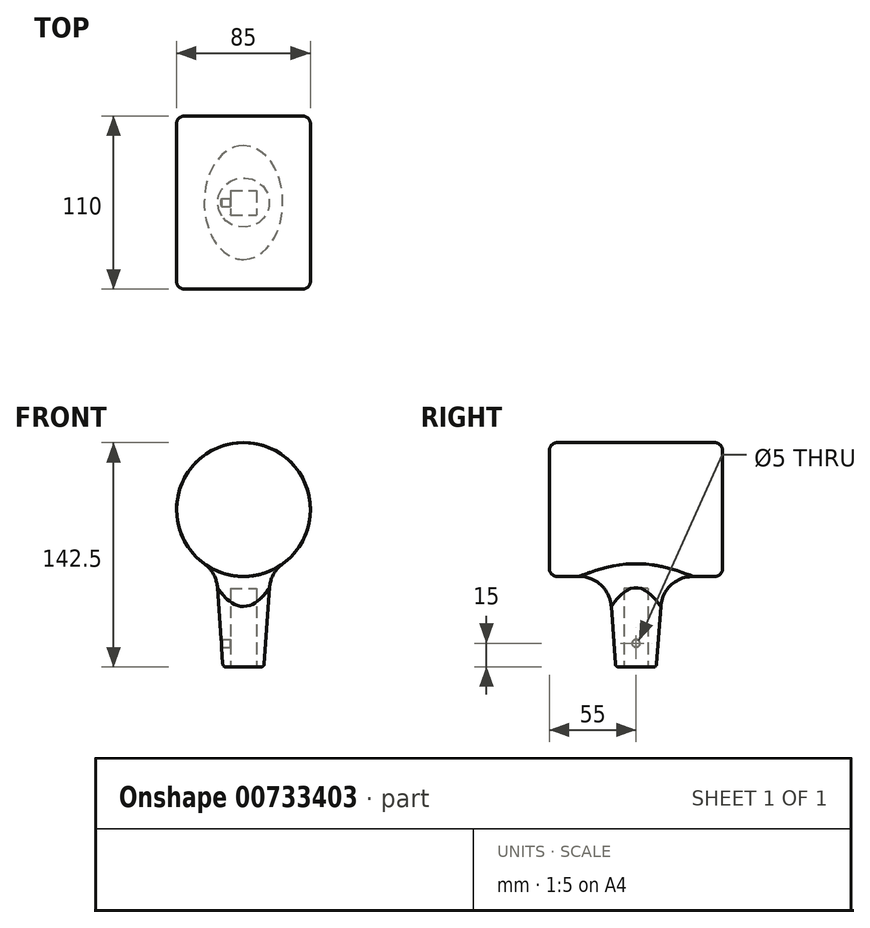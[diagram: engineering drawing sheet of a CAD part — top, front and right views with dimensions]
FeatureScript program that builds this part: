
annotation { "Feature Type Name" : "Feature", "Feature Type Description" : "" }
export const myFeature = defineFeature(function(context is Context, id is Id, definition is map)
    precondition{}
    {
        {
            var Q0;
            Q0=qCreatedBy(makeId("Front.planeOp"),FACE);
            var sketch = newSketch(context, id + "F0", { "sketchPlane" : qUnion([Q0])});
            skCircle(sketch, "E0", {"center": v(0, 0) * mm, "radius": 42.5 * mm});
            skSolve(sketch);
        }
        {
            var Q0;
            Q0=makeQuery(id+"F0.imprint","IMPRINT",FACE,{"disambiguationData":[TD([[makeQuery(id+"F0.imprint","IMPRINT",EDGE,{"derivedFrom":sQuery(id+"F0.wireOp",EDGE,"E0")}),1.0]])]});
            extrude(context, id + "F1", {"entities" : qUnion([Q0]), "endBound" : BoundingType.SYMMETRIC, "depth" : 110 * mm, "offsetDistance" : 25 * mm});
        }
        {
            var Q0;
            Q0=qCreatedBy(makeId("Top.planeOp"),FACE);
            var sketch = newSketch(context, id + "F2", { "sketchPlane" : qUnion([Q0])});
            skCircle(sketch, "E1", {"center": v(0, 0) * mm, "radius": 20 * mm});
            skSolve(sketch);
        }
        {
            var Q0;
            Q0 = qSketchRegion(id + "F2", true);
            extrude(context, id + "F3", {"entities" : qUnion([Q0]), "operationType" : NewBodyOperationType.ADD, "oppositeDirection" : true, "depth" : 100 * mm, "offsetDistance" : 25 * mm, "hasDraft" : true, "draftAngle" : 4 * degree, "draftPullDirection" : true});
        }
        {
            var Q0;
            Q0=makeQuery(id+"F3.opExtrude","CAP_FACE",FACE,{"disambiguationData":[OSD([sQuery(id+"F2.wireOp",EDGE,"E1")])],"isStart":false});
            var sketch = newSketch(context, id + "F4", { "sketchPlane" : qUnion([Q0])});
            skLineSegment(sketch, "E2.bottom", {"start": v(-8.26, -7.6) * mm, "end": v(8.15, -7.6) * mm});
            skLineSegment(sketch, "E2.top", {"start": v(-8.26, 7.8) * mm, "end": v(8.15, 7.8) * mm});
            skLineSegment(sketch, "E2.left", {"start": v(-8.26, -7.6) * mm, "end": v(-8.26, 7.8) * mm});
            skLineSegment(sketch, "E2.right", {"start": v(8.15, -7.6) * mm, "end": v(8.15, 7.8) * mm});
            skSolve(sketch);
        }
        {
            var Q0;
            Q0 = qSketchRegion(id + "F4", true);
            extrude(context, id + "F5", {"entities" : qUnion([Q0]), "operationType" : NewBodyOperationType.REMOVE, "oppositeDirection" : true, "depth" : 50 * mm, "offsetDistance" : 25 * mm});
        }
        {
            var Q0;
            Q0=qCreatedBy(makeId("Right.planeOp"),FACE);
            var sketch = newSketch(context, id + "F6", { "sketchPlane" : qUnion([Q0])});
            skCircle(sketch, "E3", {"center": v(0, -85) * mm, "radius": 2.5 * mm});
            skSolve(sketch);
        }
        {
            var Q0;
            Q0 = qSketchRegion(id + "F6", true);
            extrude(context, id + "F7", {"entities" : qUnion([Q0]), "operationType" : NewBodyOperationType.REMOVE, "oppositeDirection" : true, "depth" : 50 * mm, "offsetDistance" : 25 * mm});
        }
        {
            var Q0;
            Q0=makeQuery(id+"F1.opExtrude","CAP_EDGE",EDGE,{"disambiguationData":[OSD([sQuery(id+"F0.wireOp",EDGE,"E0")])],"isStart":true});
            fillet(context, id + "F8", {"entities" : qUnion([Q0]), "radius" : 5 * mm, "tangentPropagation" : true, "allowEdgeOverflow" : false});
        }
        {
            var Q0;
            Q0=makeQuery(id+"F1.opExtrude","CAP_EDGE",EDGE,{"disambiguationData":[OSD([sQuery(id+"F0.wireOp",EDGE,"E0")])],"isStart":false});
            fillet(context, id + "F9", {"entities" : qUnion([Q0]), "radius" : 5 * mm, "tangentPropagation" : true, "allowEdgeOverflow" : false});
        }
        {
            var Q0;
            Q0=makeQuery(id+"F3.boolean.opBoolean","INTERSECT",EDGE,{"derivedFrom":[makeQuery(id+"F1.opExtrude","SWEPT_FACE",FACE,{"disambiguationData":[OSD([sQuery(id+"F0.wireOp",EDGE,"E0")])]}),makeQuery(id+"F3.opExtrude","SWEPT_FACE",FACE,{"disambiguationData":[OSD([sQuery(id+"F2.wireOp",EDGE,"E1")])]})]});
            fillet(context, id + "F10", {"entities" : qUnion([Q0]), "radius" : 20.5 * mm, "tangentPropagation" : true, "allowEdgeOverflow" : false});
        }
        {
            var Q0;
            Q0=makeQuery(id+"F3.opExtrude","CAP_EDGE",EDGE,{"disambiguationData":[OSD([sQuery(id+"F2.wireOp",EDGE,"E1")])],"isStart":false});
            fillet(context, id + "F11", {"entities" : qUnion([Q0]), "radius" : 2 * mm, "tangentPropagation" : true, "allowEdgeOverflow" : false});
        }
    });
